annotation { "Feature Type Name" : "Feature", "Feature Type Description" : "" }
export const myFeature = defineFeature(function(context is Context, id is Id, definition is map)
    precondition{}
    {
        {
            var Q0;
            Q0=qCreatedBy(makeId("Front.planeOp"),FACE);
            var sketch = newSketch(context, id + "F0", { "sketchPlane" : qUnion([Q0])});
            skText(sketch, "E0", { "text": "PRINCE OF PEACE", "fontName": "NotoSansCJKjp-Regular.otf"});
            skText(sketch, "E1", { "text": "CATHOLIC CHURCH", "fontName": "NotoSansCJKjp-Bold.otf"});
            skText(sketch, "E2", { "text": "Fr. Carlos Cifuentes", "fontName": "NotoSansCJKjp-Bold.otf"});
            const initialGuessF0  = {"E0": [-0.0562, -0.00188, 1, 0, 0.01422], "E1": [-0.05618, -0.01103, 1, 0, 0.00626], "E2": [-0.05615, -0.02278, 1, 0, 0.0072]};
            skSetInitialGuess(sketch, initialGuessF0);
            skSolve(sketch);
        }
        {
            var Q0;
            Q0=qCreatedBy(makeId("Front.planeOp"),FACE);
            var sketch = newSketch(context, id + "F1", { "sketchPlane" : qUnion([Q0])});
            skCircle(sketch, "E3", {"center": v(-83.28, -1.16) * mm, "radius": 21.16 * mm});
            skFitSpline(sketch, "E4", {"points": [v(-96.64, 12.1) * mm, v(-90.35, 11.98) * mm, v(-84.54, 11.51) * mm], "startDerivative": vector(26.11, 1.02) * mm, "endDerivative": vector(16.7, -2.9) * mm});
            skLineSegment(sketch, "E5", {"start": v(-96.64, 12.1) * mm, "end": v(-96.64, 9.07) * mm});
            skFitSpline(sketch, "E6", {"points": [v(-96.64, 9.07) * mm, v(-90.65, 9.07) * mm, v(-84.42, 9.07) * mm], "startDerivative": vector(21.19, 2.12) * mm, "endDerivative": vector(18.28, -1.38) * mm});
            skLineSegment(sketch, "E7", {"start": v(-84.54, 11.51) * mm, "end": v(-85.35, 19.9) * mm});
            skFitSpline(sketch, "E8", {"points": [v(-82.33, 19.98) * mm, v(-81.8, 15.35) * mm, v(-81.45, 11.17) * mm], "startDerivative": vector(2.08, -14.49) * mm, "endDerivative": vector(1.43, -17.91) * mm});
            skFitSpline(sketch, "E9", {"points": [v(-81.45, 11.17) * mm, v(-76.57, 10.64) * mm, v(-71.57, 9.71) * mm], "startDerivative": vector(11.62, 0) * mm, "endDerivative": vector(12.8, -3.46) * mm});
            skLineSegment(sketch, "E10", {"start": v(-71.57, 9.71) * mm, "end": v(-71.57, 7.73) * mm});
            skFitSpline(sketch, "E11", {"points": [v(-81.28, 8.6) * mm, v(-76.45, 8.37) * mm, v(-71.57, 7.73) * mm], "startDerivative": vector(17.02, 0.7) * mm, "endDerivative": vector(11.34, -2.4) * mm});
            skFitSpline(sketch, "E12", {"points": [v(-92.4, 9.19) * mm, v(-88.9, 5.46) * mm, v(-83.72, 2.96) * mm], "startDerivative": vector(7.21, -11.16) * mm, "endDerivative": vector(14.24, -4.07) * mm});
            skFitSpline(sketch, "E13", {"points": [v(-90.1, 9.07) * mm, v(-87.56, 6.4) * mm, v(-83.84, 4.94) * mm], "startDerivative": vector(4.73, -6.1) * mm, "endDerivative": vector(7.84, -2.2) * mm});
            skLineSegment(sketch, "E14", {"start": v(-84.42, 9.07) * mm, "end": v(-83.84, 4.94) * mm});
            skFitSpline(sketch, "E15", {"points": [v(-81.28, 8.6) * mm, v(-82.33, 6.1) * mm, v(-80.47, 7.62) * mm, v(-79.13, 4.53) * mm], "startDerivative": vector(-2.09, -9.92) * mm, "endDerivative": vector(-4, -17.51) * mm});
            skFitSpline(sketch, "E16", {"points": [v(-79.13, 4.53) * mm, v(-76.22, 5.64) * mm, v(-74.35, 8.16) * mm], "startDerivative": vector(6.35, 1.51) * mm, "endDerivative": vector(3.2, 5.73) * mm});
            skFitSpline(sketch, "E17", {"points": [v(-78.95, 2.56) * mm, v(-75.23, 4.48) * mm, v(-72.93, 7.98) * mm], "startDerivative": vector(8.6, 2.96) * mm, "endDerivative": vector(3.87, 7.85) * mm});
            skFitSpline(sketch, "E18", {"points": [v(-83.72, 2.96) * mm, v(-81.92, -22.28) * mm], "startDerivative": vector(2.8, -15.7) * mm, "endDerivative": vector(2.1, -32.98) * mm});
            skFitSpline(sketch, "E19", {"points": [v(-78.95, 2.56) * mm, v(-78.95, -2.5) * mm, v(-78.95, -9.48) * mm], "startDerivative": vector(-1.5, -11.26) * mm, "endDerivative": vector(-6.14, -22.3) * mm});
            skFitSpline(sketch, "E20", {"points": [v(-78.95, -9.48) * mm, v(-79.36, -14.72) * mm, v(-79.65, -18.44) * mm], "startDerivative": vector(-0.32, -15.69) * mm, "endDerivative": vector(0, -14.2) * mm});
            skFitSpline(sketch, "E21", {"points": [v(-79.65, -18.44) * mm, v(-80.52, -19.2) * mm, v(-78.78, -21.84) * mm], "startDerivative": vector(-6.95, 0) * mm, "endDerivative": vector(4.2, -17.5) * mm});
            skArc(sketch, "E22", {"start": v(-80.33, -22.12) * mm, "mid": v(-85.43, 19.9) * mm, "end": v(-81.92, -22.28) * mm});
            skArc(sketch, "E23", {"start": v(-85.35, 19.9) * mm, "mid": v(-81.94, -22.28) * mm, "end": v(-83.87, 20) * mm});
            skSolve(sketch);
        }
        {
            var Q0;
            Q0 = qSketchRegion(id + "F0", true);
            var Q1;
            Q1=makeQuery(id+"F1.imprint","IMPRINT",FACE,{"disambiguationData":[TD([[makeQuery(id+"F1.imprint","IMPRINT",EDGE,{"derivedFrom":sQuery(id+"F1.wireOp",EDGE,"E4")}),1.0]])]});
            var Q2;
            {var subQ2=sQuery(id+"F1.wireOp",EDGE,"E13");Q2=makeQuery(id+"F1.imprint","IMPRINT",FACE,{"disambiguationData":[TD([[makeQuery(id+"F1.imprint","IMPRINT",EDGE,{"derivedFrom":subQ2}),1.0]])]});}
            var Q3;
            {var subQ0=sQuery(id+"F1.wireOp",EDGE,"E15");Q3=makeQuery(id+"F1.imprint","IMPRINT",FACE,{"disambiguationData":[TD([[makeQuery(id+"F1.imprint","IMPRINT",EDGE,{"derivedFrom":subQ0}),1.0]])]});}
            var Q4;
            {var subQ1=sQuery(id+"F1.wireOp",EDGE,"E8");Q4=makeQuery(id+"F1.imprint","IMPRINT",FACE,{"disambiguationData":[TD([[makeQuery(id+"F1.imprint","IMPRINT",EDGE,{"derivedFrom":subQ1}),1.0]])]});}
            extrude(context, id + "F2", {"entities" : qUnion([Q0, Q1, Q2, Q3, Q4]), "depth" : 2 * mm});
        }
        {
            var Q0;
            Q0=qCreatedBy(makeId("Front.planeOp"),FACE);
            var sketch = newSketch(context, id + "F3", { "sketchPlane" : qUnion([Q0])});
            skLineSegment(sketch, "E24.bottom", {"start": v(-108.62, 21.73) * mm, "end": v(111.58, 21.73) * mm});
            skLineSegment(sketch, "E24.top", {"start": v(-108.62, -24.27) * mm, "end": v(111.58, -24.27) * mm});
            skLineSegment(sketch, "E24.left", {"start": v(-108.62, 21.73) * mm, "end": v(-108.62, -24.27) * mm});
            skLineSegment(sketch, "E24.right", {"start": v(111.58, 21.73) * mm, "end": v(111.58, -24.27) * mm});
            skSolve(sketch);
        }
        {
            var Q0;
            Q0 = qSketchRegion(id + "F3", true);
            extrude(context, id + "F4", {"entities" : qUnion([Q0]), "oppositeDirection" : true, "depth" : 2 * mm});
        }
    });